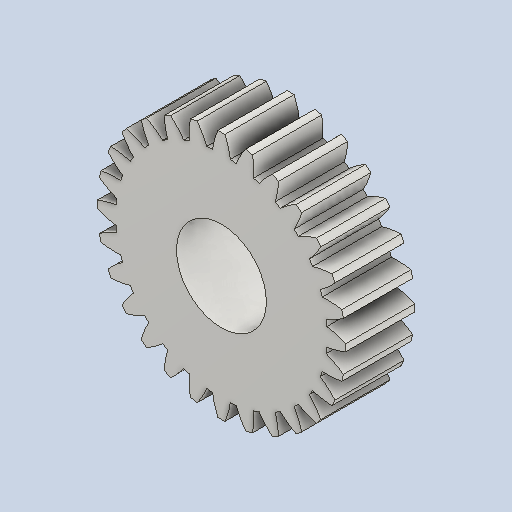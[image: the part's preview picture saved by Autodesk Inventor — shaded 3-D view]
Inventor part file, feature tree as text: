
AUTODESK INVENTOR PART (.ipt)
format: ipt  version: 2022 (Build 260153000, 153)  size: 289,792 bytes
history: native  units: mm (DEFAULTED — no unit token found)
features: plane x3, other x3, sketch x2, extrude x1
ambient origin geometry x8: Origin, YZ Plane, XZ Plane, XY Plane, X Axis, Y Axis, Z Axis, Center Point
bodies: Solid1 (feature_tree)
feature tree (9):
  extrude  "Extrusion1"  Depth=5.0mm TaperAngle=0.0deg
  plane  "Work Plane2"
  plane  "Work Plane8"
  plane  "Work Plane9"
  other  "Spur Gear"
  sketch  "Sketch1"  dims[d0=17.982731mm d1=5.0mm d2=0.0mm]
  sketch  "Sketch2"  dims[d3=16.8mm d4=10.0mm d5=0.0mm d16=17.0mm d17=0.0mm d34=1.121997mm d39=0.0mm d41=0.0mm d43=17.0mm d46=17.0mm d47=0.0mm d48=0.0mm d49=6.5mm]
  other  "Srf1"
  other  "Pitch Diameter"
